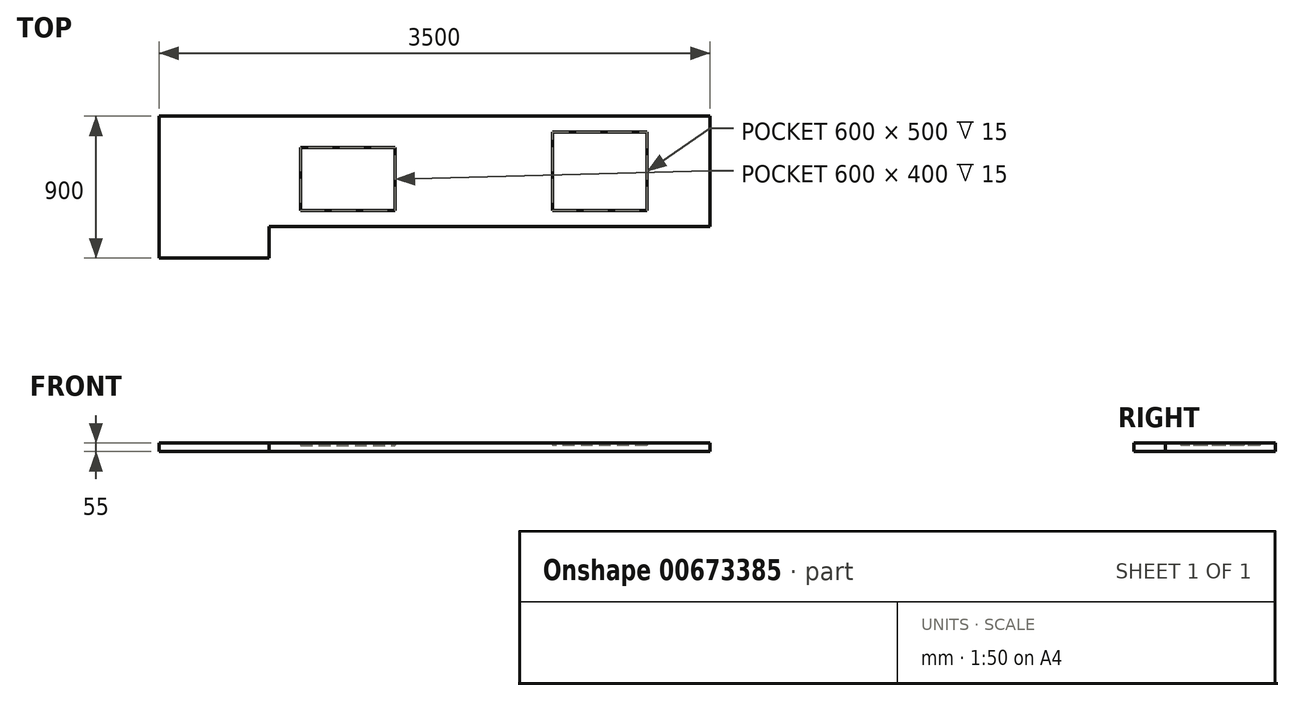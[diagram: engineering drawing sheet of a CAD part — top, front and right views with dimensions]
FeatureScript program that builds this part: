
annotation { "Feature Type Name" : "Feature", "Feature Type Description" : "" }
export const myFeature = defineFeature(function(context is Context, id is Id, definition is map)
    precondition{}
    {
        {
            var Q0;
            Q0=qCreatedBy(makeId("Top.planeOp"),FACE);
            var sketch = newSketch(context, id + "F0", { "sketchPlane" : qUnion([Q0])});
            skLineSegment(sketch, "E0.bottom", {"start": v(-744.28, 348.62) * mm, "end": v(2055.72, 348.62) * mm});
            skLineSegment(sketch, "E0.top", {"start": v(-744.28, -351.38) * mm, "end": v(2055.72, -351.38) * mm});
            skLineSegment(sketch, "E0.right", {"start": v(2055.72, 348.62) * mm, "end": v(2055.72, -351.38) * mm});
            skLineSegment(sketch, "E1.bottom", {"start": v(-744.28, 348.62) * mm, "end": v(-1444.28, 348.62) * mm});
            skLineSegment(sketch, "E1.top", {"start": v(-744.28, -551.38) * mm, "end": v(-1444.28, -551.38) * mm});
            skLineSegment(sketch, "E1.left", {"start": v(-744.28, -351.38) * mm, "end": v(-744.28, -551.38) * mm});
            skLineSegment(sketch, "E1.right", {"start": v(-1444.28, 348.62) * mm, "end": v(-1444.28, -551.38) * mm});
            skSolve(sketch);
        }
        {
            var Q0;
            Q0=makeQuery(id+"F0.imprint","IMPRINT",FACE,{"disambiguationData":[TD([[makeQuery(id+"F0.imprint","IMPRINT",EDGE,{"derivedFrom":sQuery(id+"F0.wireOp",EDGE,"E0.bottom")}),-1.0]])]});
            extrude(context, id + "F1", {"entities" : qUnion([Q0]), "depth" : 40 * mm, "offsetDistance" : 25 * mm});
        }
        {
            var Q0;
            Q0=makeQuery(id+"F1.opExtrude","CAP_FACE",FACE,{"disambiguationData":[OSD([sQuery(id+"F0.wireOp",EDGE,"E0.bottom"),sQuery(id+"F0.wireOp",EDGE,"E0.top"),sQuery(id+"F0.wireOp",EDGE,"E0.left"),sQuery(id+"F0.wireOp",EDGE,"E0.right")])],"isStart":false});
            var sketch = newSketch(context, id + "F2", { "sketchPlane" : qUnion([Q0])});
            skLineSegment(sketch, "E2.bottom", {"start": v(1655.72, 248.62) * mm, "end": v(1055.72, 248.62) * mm});
            skLineSegment(sketch, "E2.top", {"start": v(1655.72, -251.38) * mm, "end": v(1055.72, -251.38) * mm});
            skLineSegment(sketch, "E2.left", {"start": v(1655.72, 248.62) * mm, "end": v(1655.72, -251.38) * mm});
            skLineSegment(sketch, "E2.right", {"start": v(1055.72, 248.62) * mm, "end": v(1055.72, -251.38) * mm});
            skLineSegment(sketch, "E3.bottom", {"start": v(-544.28, 148.62) * mm, "end": v(55.72, 148.62) * mm});
            skLineSegment(sketch, "E3.top", {"start": v(-544.28, -251.38) * mm, "end": v(55.72, -251.38) * mm});
            skLineSegment(sketch, "E3.left", {"start": v(-544.28, 148.62) * mm, "end": v(-544.28, -251.38) * mm});
            skLineSegment(sketch, "E3.right", {"start": v(55.72, 148.62) * mm, "end": v(55.72, -251.38) * mm});
            skSolve(sketch);
        }
        {
            var Q0;
            Q0=makeQuery(id+"F2.imprint","IMPRINT",FACE,{"disambiguationData":[TD([[makeQuery(id+"F2.imprint","IMPRINT",EDGE,{"derivedFrom":sQuery(id+"F2.wireOp",EDGE,"E2.bottom")}),-1.0]])]});
            extrude(context, id + "F3", {"entities" : qUnion([Q0]), "operationType" : NewBodyOperationType.ADD, "depth" : 15 * mm, "offsetDistance" : 25 * mm});
        }
    });
